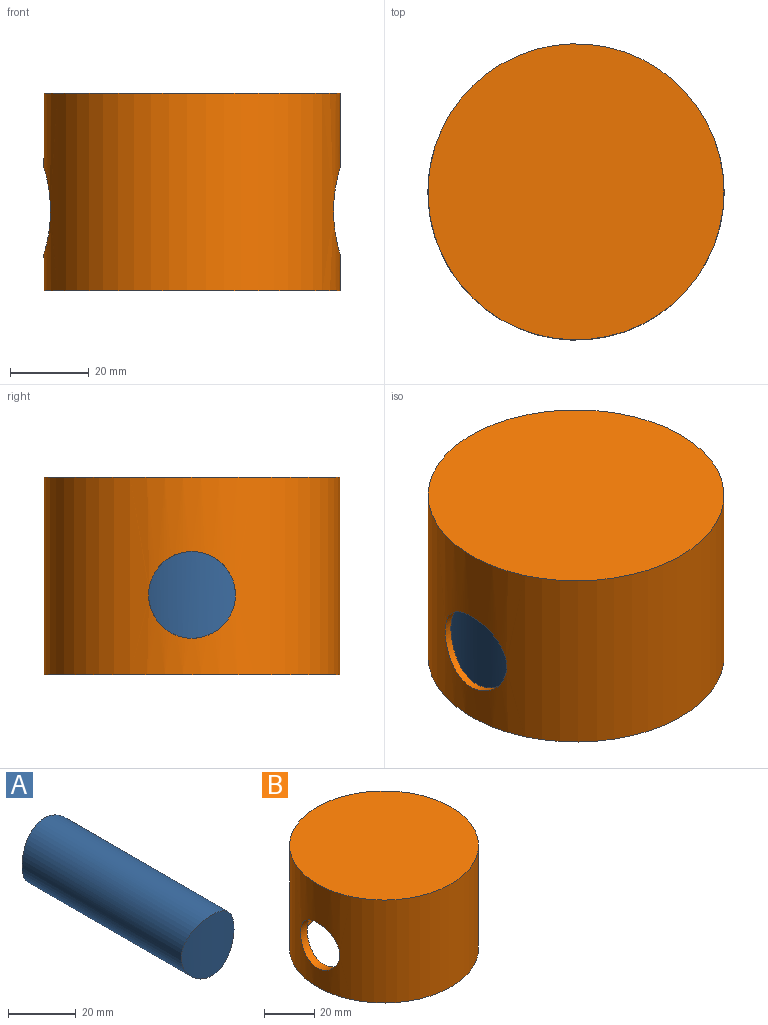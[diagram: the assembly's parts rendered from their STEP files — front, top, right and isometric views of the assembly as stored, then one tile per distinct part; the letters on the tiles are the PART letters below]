
ASSEMBLY  parts=2 mates=1
PART A: 3 faces, bbox 22x70x22 mm
  f0: cylinder r=11mm len=70mm, axis (0,-1,0), area 4716.2mm2, adj f1,f2
  f1: cylinder r=35mm len=22mm, axis (0,0,-1), area 385mm2, adj f0
  f2: cylinder r=35mm len=22mm, axis (0,0,-1), area 385mm2, adj f0
PART B: 7 faces, bbox 75x75x50 mm
  f0: cylinder r=37.5mm len=75mm, axis (0,0,-1), area 11012mm2, adj f1,f2,f5,f6
  f1: plane 75x75mm, normal (0,0,1), area 4417.9mm2, adj f0
  f2: plane 75x75mm, normal (0,0,-1), area 786.2mm2, adj f0,f3
  f3: cylinder r=34mm len=68mm, axis (0,0,-1), area 7347.5mm2, adj f2,f4,f5,f6
  f4: plane 68x68mm, normal (0,0,-1), area 3631.7mm2, adj f3
  f5: cylinder r=11mm len=22mm, axis (1,0,0), area 248mm2, adj f0,f3
  f6: cylinder r=11mm len=22mm, axis (1,0,0), area 248mm2, adj f0,f3
PLACE A rot(axis=(0.71,0.71,0),180deg) t=(-18.89,-19.62,21.27)mm
PLACE B rot(axis=(0.66,-0.76,0),0deg) t=(16.72,-19.62,1.06)mm
MATE fastened A.f0 <-> B.f5  axis (-1,0,0) through (51.55,-19.62,21.27)mm
